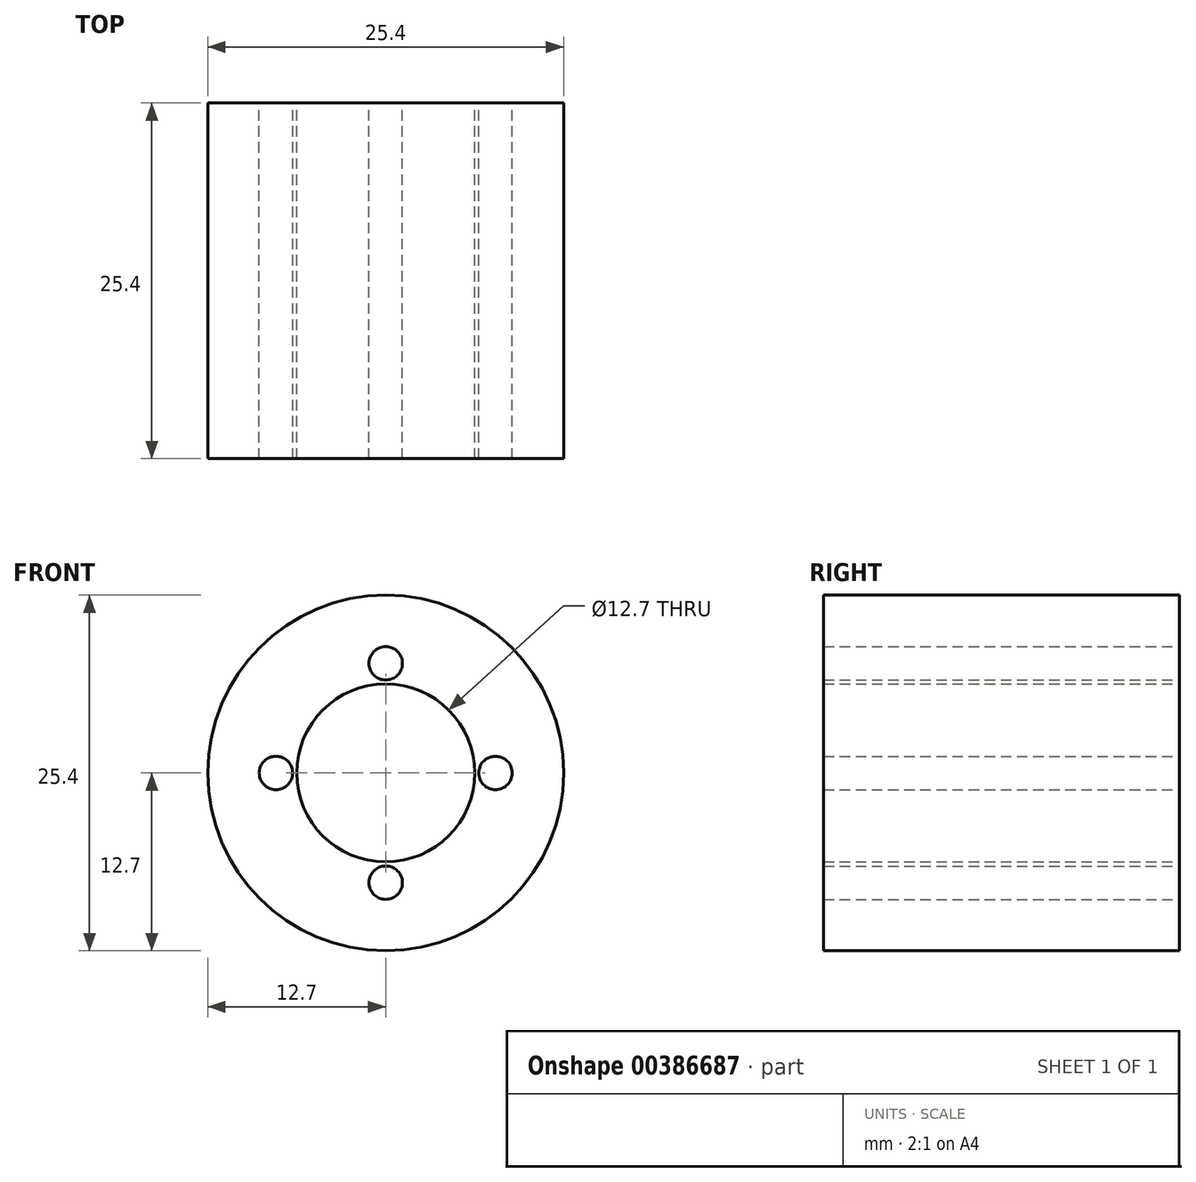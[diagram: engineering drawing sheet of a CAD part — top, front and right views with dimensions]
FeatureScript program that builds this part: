
annotation { "Feature Type Name" : "Feature", "Feature Type Description" : "" }
export const myFeature = defineFeature(function(context is Context, id is Id, definition is map)
    precondition{}
    {
        {
            var Q0;
            Q0=qCreatedBy(makeId("Front.planeOp"),FACE);
            var sketch = newSketch(context, id + "F0", { "sketchPlane" : qUnion([Q0])});
            skCircle(sketch, "E0", {"center": v(0, 0) * mm, "radius": 12.7 * mm});
            skCircle(sketch, "E1", {"center": v(0, 0) * mm, "radius": 9.53 * mm, "construction": true});
            skCircle(sketch, "E2", {"center": v(0, 0) * mm, "radius": 6.35 * mm});
            skCircle(sketch, "E3", {"center": v(0, 7.83) * mm, "radius": 1.2 * mm});
            skCircle(sketch, "E4.1.0", {"center": v(-7.83, 0) * mm, "radius": 1.2 * mm});
            skCircle(sketch, "E4.2.0", {"center": v(0, -7.83) * mm, "radius": 1.2 * mm});
            skCircle(sketch, "E4.3.0", {"center": v(7.83, 0) * mm, "radius": 1.2 * mm});
            skSolve(sketch);
        }
        {
            var Q0;
            Q0=makeQuery(id+"F0.imprint","IMPRINT",FACE,{"disambiguationData":[TD([[makeQuery(id+"F0.imprint","IMPRINT",EDGE,{"derivedFrom":sQuery(id+"F0.wireOp",EDGE,"E0")}),1.0]])]});
            extrude(context, id + "F1", {"entities" : qUnion([Q0]), "depth" : 25.4 * mm});
        }
    });
